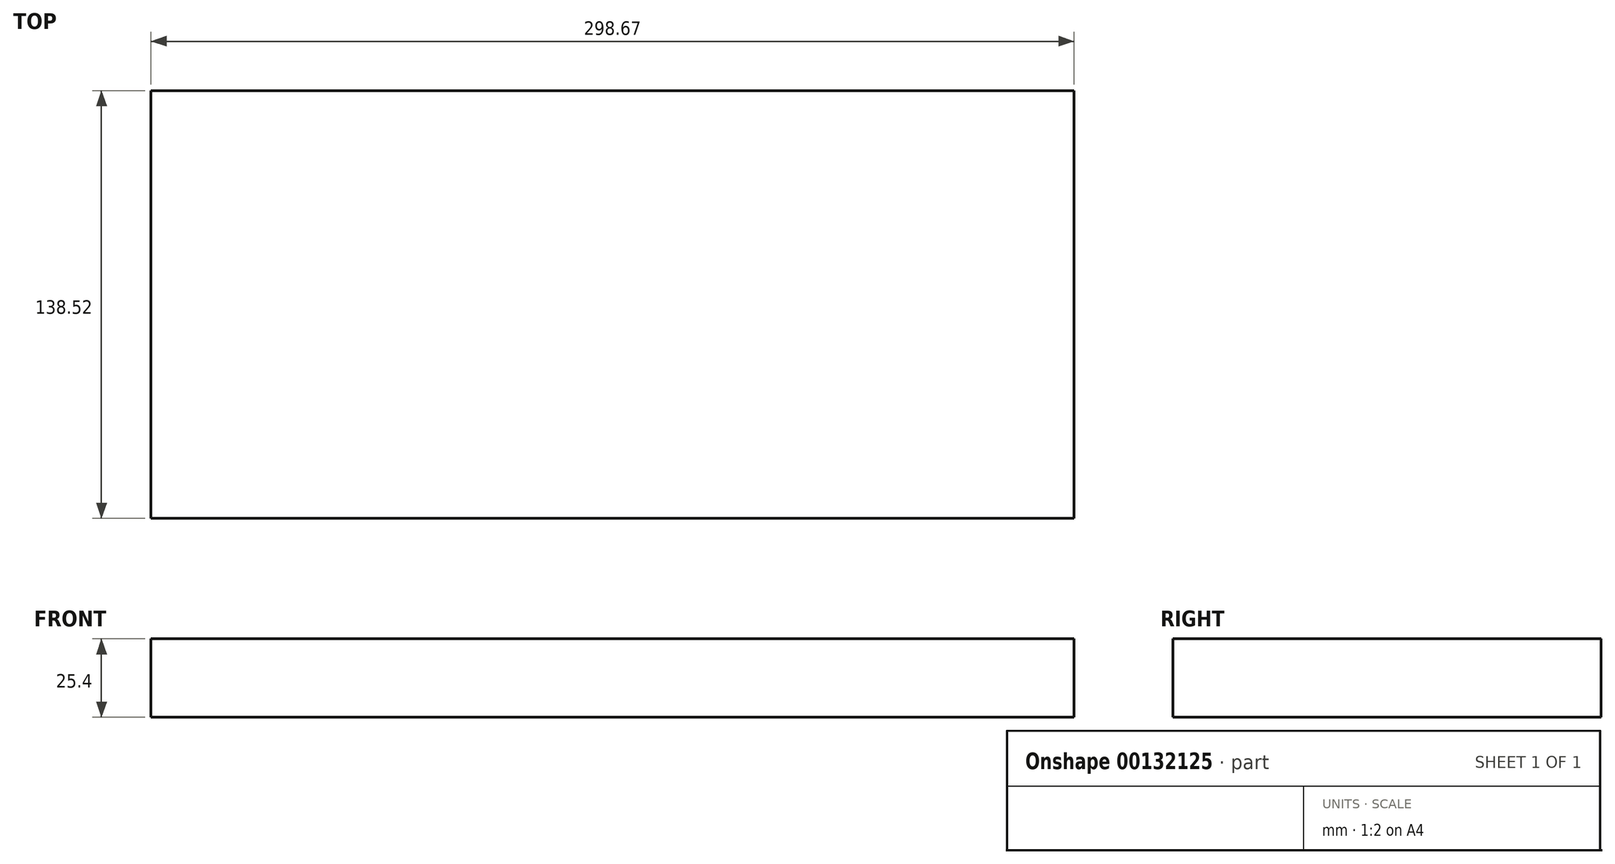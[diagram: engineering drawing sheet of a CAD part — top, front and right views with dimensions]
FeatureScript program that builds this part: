
annotation { "Feature Type Name" : "Feature", "Feature Type Description" : "" }
export const myFeature = defineFeature(function(context is Context, id is Id, definition is map)
    precondition{}
    {
        {
            var Q0;
            Q0=qCreatedBy(makeId("Top.planeOp"),FACE);
            var sketch = newSketch(context, id + "F0", { "sketchPlane" : qUnion([Q0])});
            skLineSegment(sketch, "E0.bottom", {"start": v(-157.58, 69.6) * mm, "end": v(141.09, 69.6) * mm});
            skLineSegment(sketch, "E0.top", {"start": v(-157.58, -68.92) * mm, "end": v(141.09, -68.92) * mm});
            skLineSegment(sketch, "E0.left", {"start": v(-157.58, 69.6) * mm, "end": v(-157.58, -68.92) * mm});
            skLineSegment(sketch, "E0.right", {"start": v(141.09, 69.6) * mm, "end": v(141.09, -68.92) * mm});
            skSolve(sketch);
        }
        {
            var Q0;
            Q0=makeQuery(id+"F0.imprint","IMPRINT",FACE,{"disambiguationData":[TD([[makeQuery(id+"F0.imprint","IMPRINT",EDGE,{"derivedFrom":sQuery(id+"F0.wireOp",EDGE,"E0.bottom")}),-1.0]])]});
            extrude(context, id + "F1", {"entities" : qUnion([Q0]), "depth" : 25.4 * mm});
        }
    });
